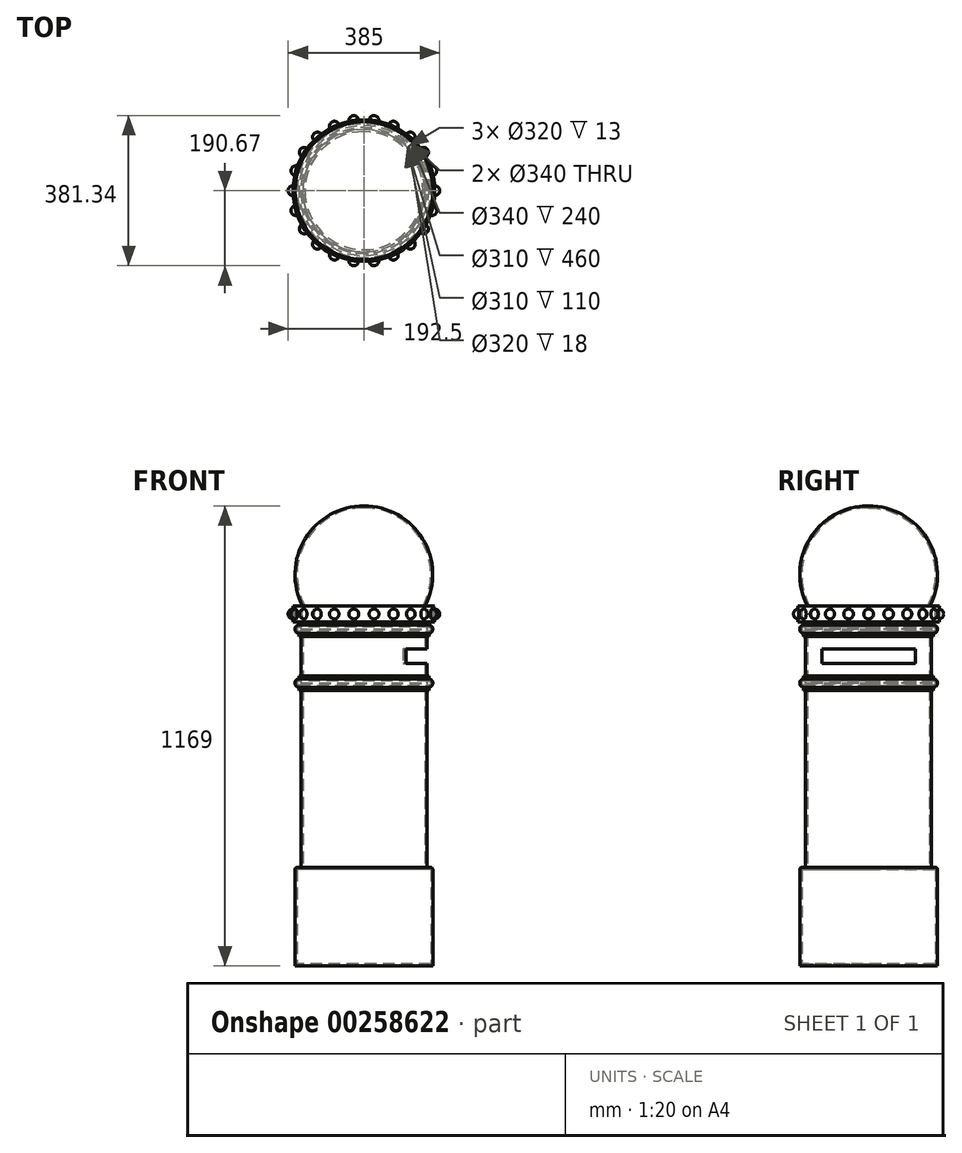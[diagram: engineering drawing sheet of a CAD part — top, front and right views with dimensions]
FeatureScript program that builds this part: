
annotation { "Feature Type Name" : "Feature", "Feature Type Description" : "" }
export const myFeature = defineFeature(function(context is Context, id is Id, definition is map)
    precondition{}
    {
        {
            var Q0;
            Q0=qCreatedBy(makeId("Top.planeOp"),FACE);
            var sketch = newSketch(context, id + "F0", { "sketchPlane" : qUnion([Q0])});
            skCircle(sketch, "E0", {"center": v(0, 0) * mm, "radius": 175 * mm});
            skSolve(sketch);
        }
        {
            var Q0;
            Q0 = qSketchRegion(id + "F0", true);
            extrude(context, id + "F1", {"entities" : qUnion([Q0]), "depth" : 250 * mm});
        }
        {
            var Q0;
            Q0=makeQuery(id+"F1.opExtrude","CAP_FACE",FACE,{"disambiguationData":[OSD([sQuery(id+"F0.wireOp",EDGE,"E0")])],"isStart":false});
            var sketch = newSketch(context, id + "F2", { "sketchPlane" : qUnion([Q0])});
            skCircle(sketch, "E1", {"center": v(0, 0) * mm, "radius": 160 * mm});
            skSolve(sketch);
        }
        {
            var Q0;
            Q0 = qSketchRegion(id + "F2", true);
            extrude(context, id + "F3", {"entities" : qUnion([Q0]), "operationType" : NewBodyOperationType.ADD, "depth" : 450 * mm});
        }
        {
            var Q0;
            Q0=makeQuery(id+"F1.opExtrude","CAP_EDGE",EDGE,{"disambiguationData":[OSD([sQuery(id+"F0.wireOp",EDGE,"E0")])],"isStart":false});
            fillet(context, id + "F4", {"entities" : qUnion([Q0]), "radius" : 5 * mm, "tangentPropagation" : true, "allowEdgeOverflow" : false});
        }
        {
            var Q0;
            Q0=makeQuery(id+"F3.opExtrude","CAP_FACE",FACE,{"disambiguationData":[OSD([sQuery(id+"F2.wireOp",EDGE,"E1")])],"isStart":false});
            var sketch = newSketch(context, id + "F5", { "sketchPlane" : qUnion([Q0])});
            skCircle(sketch, "E2", {"center": v(0, 0) * mm, "radius": 165 * mm});
            skSolve(sketch);
        }
        {
            var Q0;
            Q0=makeQuery(id+"F5.imprint","IMPRINT",FACE,{"disambiguationData":[TD([[makeQuery(id+"F5.imprint","IMPRINT",EDGE,{"derivedFrom":sQuery(id+"F5.wireOp",EDGE,"E2")}),1.0]])]});
            var Q1;
            Q1=makeQuery(id+"F5.imprint","IMPRINT",FACE,{"disambiguationData":[TD([[makeQuery(id+"F5.imprint","IMPRINT",EDGE,{"derivedFrom":makeQuery(id+"F3.opExtrude","CAP_EDGE",EDGE,{"disambiguationData":[OSD([sQuery(id+"F2.wireOp",EDGE,"E1")])],"isStart":false})}),1.0]])]});
            extrude(context, id + "F6", {"entities" : qUnion([Q0, Q1]), "operationType" : NewBodyOperationType.ADD, "depth" : 8 * mm});
        }
        {
            var Q0;
            Q0=makeQuery(id+"F6.opExtrude","CAP_FACE",FACE,{"disambiguationData":[OSD([sQuery(id+"F5.wireOp",EDGE,"E2")])],"isStart":false});
            var sketch = newSketch(context, id + "F7", { "sketchPlane" : qUnion([Q0])});
            skCircle(sketch, "E3", {"center": v(0, 0) * mm, "radius": 175 * mm});
            skSolve(sketch);
        }
        {
            var Q0;
            Q0 = qSketchRegion(id + "F7", true);
            extrude(context, id + "F8", {"entities" : qUnion([Q0]), "operationType" : NewBodyOperationType.ADD, "depth" : 21 * mm});
        }
        {
            var Q0;
            Q0=makeQuery(id+"F8.opExtrude","CAP_FACE",FACE,{"disambiguationData":[OSD([sQuery(id+"F7.wireOp",EDGE,"E3")])],"isStart":false});
            var sketch = newSketch(context, id + "F9", { "sketchPlane" : qUnion([Q0])});
            skCircle(sketch, "E4", {"center": v(0, 0) * mm, "radius": 165 * mm});
            skSolve(sketch);
        }
        {
            var Q0;
            Q0=makeQuery(id+"F9.imprint","IMPRINT",FACE,{"disambiguationData":[TD([[makeQuery(id+"F9.imprint","IMPRINT",EDGE,{"derivedFrom":sQuery(id+"F9.wireOp",EDGE,"E4")}),1.0]])]});
            extrude(context, id + "F10", {"entities" : qUnion([Q0]), "operationType" : NewBodyOperationType.ADD, "depth" : 8 * mm});
        }
        {
            var Q0;
            Q0=makeQuery(id+"F8.opExtrude","CAP_EDGE",EDGE,{"disambiguationData":[OSD([sQuery(id+"F7.wireOp",EDGE,"E3")])],"isStart":false});
            var Q1;
            Q1=makeQuery(id+"F8.opExtrude","CAP_EDGE",EDGE,{"disambiguationData":[OSD([sQuery(id+"F7.wireOp",EDGE,"E3")])],"isStart":true});
            fillet(context, id + "F11", {"entities" : qUnion([Q0, Q1]), "radius" : 10 * mm, "tangentPropagation" : true, "allowEdgeOverflow" : false});
        }
        {
            var Q0;
            Q0=makeQuery(id+"F10.opExtrude","CAP_FACE",FACE,{"disambiguationData":[OSD([sQuery(id+"F9.wireOp",EDGE,"E4")])],"isStart":false});
            var sketch = newSketch(context, id + "F12", { "sketchPlane" : qUnion([Q0])});
            skCircle(sketch, "E5", {"center": v(0, 0) * mm, "radius": 160 * mm});
            skSolve(sketch);
        }
        {
            var Q0;
            Q0=makeQuery(id+"F12.imprint","IMPRINT",FACE,{"disambiguationData":[TD([[makeQuery(id+"F12.imprint","IMPRINT",EDGE,{"derivedFrom":sQuery(id+"F12.wireOp",EDGE,"E5")}),1.0]])]});
            extrude(context, id + "F13", {"entities" : qUnion([Q0]), "operationType" : NewBodyOperationType.ADD, "depth" : 100 * mm});
        }
        {
            var Q0;
            Q0=makeQuery(id+"F13.opExtrude","CAP_FACE",FACE,{"disambiguationData":[OSD([sQuery(id+"F12.wireOp",EDGE,"E5")])],"isStart":false});
            var sketch = newSketch(context, id + "F14", { "sketchPlane" : qUnion([Q0])});
            skCircle(sketch, "E6", {"center": v(0, 0) * mm, "radius": 165 * mm});
            skSolve(sketch);
        }
        {
            var Q0;
            Q0=makeQuery(id+"F14.imprint","IMPRINT",FACE,{"disambiguationData":[TD([[makeQuery(id+"F14.imprint","IMPRINT",EDGE,{"derivedFrom":sQuery(id+"F14.wireOp",EDGE,"E6")}),1.0]])]});
            var Q1;
            Q1=makeQuery(id+"F14.imprint","IMPRINT",FACE,{"disambiguationData":[TD([[makeQuery(id+"F14.imprint","IMPRINT",EDGE,{"derivedFrom":makeQuery(id+"F13.opExtrude","CAP_EDGE",EDGE,{"disambiguationData":[OSD([sQuery(id+"F12.wireOp",EDGE,"E5")])],"isStart":false})}),1.0]])]});
            extrude(context, id + "F15", {"entities" : qUnion([Q0, Q1]), "operationType" : NewBodyOperationType.ADD, "depth" : 8 * mm});
        }
        {
            var Q0;
            Q0=makeQuery(id+"F15.opExtrude","CAP_FACE",FACE,{"disambiguationData":[OSD([sQuery(id+"F14.wireOp",EDGE,"E6")])],"isStart":false});
            var sketch = newSketch(context, id + "F16", { "sketchPlane" : qUnion([Q0])});
            skCircle(sketch, "E7", {"center": v(0, 0) * mm, "radius": 175 * mm});
            skSolve(sketch);
        }
        {
            var Q0;
            Q0 = qSketchRegion(id + "F16", true);
            extrude(context, id + "F17", {"entities" : qUnion([Q0]), "operationType" : NewBodyOperationType.ADD, "depth" : 21 * mm});
        }
        {
            var Q0;
            Q0=makeQuery(id+"F17.opExtrude","CAP_FACE",FACE,{"disambiguationData":[OSD([sQuery(id+"F16.wireOp",EDGE,"E7")])],"isStart":false});
            var sketch = newSketch(context, id + "F18", { "sketchPlane" : qUnion([Q0])});
            skCircle(sketch, "E8", {"center": v(0, 0) * mm, "radius": 165 * mm});
            skSolve(sketch);
        }
        {
            var Q0;
            Q0 = qSketchRegion(id + "F18", true);
            extrude(context, id + "F19", {"entities" : qUnion([Q0]), "operationType" : NewBodyOperationType.ADD, "depth" : 8 * mm});
        }
        {
            var Q0;
            Q0=makeQuery(id+"F17.opExtrude","CAP_EDGE",EDGE,{"disambiguationData":[OSD([sQuery(id+"F16.wireOp",EDGE,"E7")])],"isStart":false});
            var Q1;
            Q1=makeQuery(id+"F17.opExtrude","CAP_EDGE",EDGE,{"disambiguationData":[OSD([sQuery(id+"F16.wireOp",EDGE,"E7")])],"isStart":true});
            fillet(context, id + "F20", {"entities" : qUnion([Q0, Q1]), "radius" : 10 * mm, "tangentPropagation" : true, "allowEdgeOverflow" : false});
        }
        {
            var Q0;
            Q0=makeQuery(id+"F19.opExtrude","CAP_FACE",FACE,{"disambiguationData":[OSD([sQuery(id+"F18.wireOp",EDGE,"E8")])],"isStart":false});
            shell(context, id + "F21", {"entities" : qUnion([Q0]), "thickness" : 5 * mm});
        }
        {
            var Q0;
            Q0=qCreatedBy(makeId("Right.planeOp"),FACE);
            var sketch = newSketch(context, id + "F22", { "sketchPlane" : qUnion([Q0])});
            skLineSegment(sketch, "E9.bottom", {"start": v(118.5, 805.5) * mm, "end": v(-118.5, 805.5) * mm});
            skLineSegment(sketch, "E9.top", {"start": v(118.5, 768.5) * mm, "end": v(-118.5, 768.5) * mm});
            skLineSegment(sketch, "E9.left", {"start": v(118.5, 805.5) * mm, "end": v(118.5, 768.5) * mm});
            skLineSegment(sketch, "E9.right", {"start": v(-118.5, 805.5) * mm, "end": v(-118.5, 768.5) * mm});
            skPoint(sketch, "E9.middle", {"position": v(0, 787) * mm});
            skSolve(sketch);
        }
        {
            var Q0;
            Q0=makeQuery(id+"F22.imprint","IMPRINT",FACE,{"disambiguationData":[TD([[makeQuery(id+"F22.imprint","IMPRINT",EDGE,{"derivedFrom":sQuery(id+"F22.wireOp",EDGE,"E9.bottom")}),1.0]])]});
            extrude(context, id + "F23", {"entities" : qUnion([Q0]), "operationType" : NewBodyOperationType.REMOVE, "depth" : 566 * mm});
        }
        {
            var Q0;
            Q0=makeQuery(id+"F19.opExtrude","CAP_FACE",FACE,{"disambiguationData":[OSD([sQuery(id+"F18.wireOp",EDGE,"E8")])],"isStart":false});
            var sketch = newSketch(context, id + "F24", { "sketchPlane" : qUnion([Q0])});
            skCircle(sketch, "E10", {"center": v(0, 0) * mm, "radius": 180 * mm});
            skSolve(sketch);
        }
        {
            var Q0;
            Q0 = qSketchRegion(id + "F24", true);
            extrude(context, id + "F25", {"entities" : qUnion([Q0]), "operationType" : NewBodyOperationType.ADD, "depth" : 40 * mm});
        }
        {
            var Q0;
            Q0=qCreatedBy(makeId("Right.planeOp"),FACE);
            cPlane(context, id + "F26", {"entities" : qUnion([Q0]), "cplaneType" : CPlaneType.OFFSET, "offset" : 180 * mm, "width" : 150 * mm, "height" : 150 * mm});
        }
        {
            var Q0;
            Q0=qCreatedBy(id+"F26.planeOp",FACE);
            var sketch = newSketch(context, id + "F27", { "sketchPlane" : qUnion([Q0])});
            skCircle(sketch, "E11", {"center": v(0, 894) * mm, "radius": 12.5 * mm});
            skLineSegment(sketch, "E12", {"start": v(0, 894) * mm, "end": v(12.5, 894) * mm});
            skLineSegment(sketch, "E13", {"start": v(0, 894) * mm, "end": v(-12.5, 894) * mm});
            skSolve(sketch);
        }
        {
            var Q0;
            {var subQ0=sQuery(id+"F27.wireOp",EDGE,"E12");Q0=makeQuery(id+"F27.imprint","IMPRINT",FACE,{"disambiguationData":[TD([[makeQuery(id+"F27.imprint","IMPRINT",EDGE,{"derivedFrom":subQ0}),1.0]])]});}
            var Q1;
            Q1=sQuery(id+"F27.wireOp",EDGE,"E12");
            revolve(context, id + "F28", {"operationType" : NewBodyOperationType.ADD, "entities" : qUnion([Q0]), "axis" : qUnion([Q1]), "revolveType" : RevolveType.ONE_DIRECTION, "angle" : 180 * degree});
        }
        {
            var Q0;
            Q0=makeQuery(id+"F28.opRevolve","SWEPT_BODY",BODY,{"disambiguationData":[OSD([sQuery(id+"F27.wireOp",EDGE,"E11"),sQuery(id+"F27.wireOp",EDGE,"E12"),sQuery(id+"F27.wireOp",EDGE,"E13")])]});
            var Q1;
            Q1=makeQuery(id+"F25.opExtrude","CAP_EDGE",EDGE,{"disambiguationData":[OSD([sQuery(id+"F24.wireOp",EDGE,"E10")])],"isStart":false});
            circularPattern(context, id + "F29", {"entities" : qUnion([Q0]), "axis" : qUnion([Q1]), "angle" : 360 * degree, "instanceCount" : 22, "oppositeDirection" : true, "equalSpace" : true});
        }
        {
            var Q0;
            Q0=qCreatedBy(makeId("Right.planeOp"),FACE);
            var sketch = newSketch(context, id + "F30", { "sketchPlane" : qUnion([Q0])});
            skArc(sketch, "E14", {"start": v(0, 1169) * mm, "mid": v(-149.35, 1085.21) * mm, "end": v(-155.69, 914.08) * mm});
            skLineSegment(sketch, "E15", {"start": v(-150.04, 914.08) * mm, "end": v(-155.69, 914.08) * mm});
            skLineSegment(sketch, "E16", {"start": v(0, 914.08) * mm, "end": v(0, 1169) * mm});
            skPoint(sketch, "E17.orphan", {"position": v(155.69, 914.08) * mm});
            skArc(sketch, "E18", {"start": v(0, 1164) * mm, "mid": v(-145.75, 1081.5) * mm, "end": v(-150.04, 914.08) * mm});
            skSolve(sketch);
        }
        {
            var Q0;
            {var subQ0=sQuery(id+"F30.wireOp",EDGE,"E14");Q0=makeQuery(id+"F30.imprint","IMPRINT",FACE,{"disambiguationData":[TD([[makeQuery(id+"F30.imprint","IMPRINT",EDGE,{"derivedFrom":subQ0}),1.0]])]});}
            var Q1;
            Q1=sQuery(id+"F30.wireOp",EDGE,"E16");
            revolve(context, id + "F31", {"entities" : qUnion([Q0]), "axis" : qUnion([Q1]), "revolveType" : RevolveType.FULL});
        }
    });
